# Revit family: Rail-P
name_source: partatom
category: Lighting Fixtures
revit_build: Autodesk Revit 2014 (Build: 20130308_1515(x64)
units: mm (PartAtom-declared; Revit-internal decimal feet)

## types (4) — shared parameters
Apparent Load = 0 VA
Assembly Code = D5020200
Color Filter = 16777215
Default Elevation = 4' - 0"
Description = Rail LED Pendant Indirect/Direct
Dimming Lamp Color Temperature Shift = <None>
Downlight Diffuser = Soft Glow Lens/Blade Baffle with Overlay
Emit Shape Visible in Rendering = No
Emit from Rectangle Length = 0' - 2 1/2"
Fixture Distribution = Indirect/Direct
Glass = Glass - Hubbell - White
Housing Material = Paint - Hubbell - Matte White
Lamp = LED
Load Classification = Lighting
Manufacturer = Litecontrol Lighting
Model = Rail-12L
Mounting = Pendant
Photometric Link = https://www.hubbell.com
Photometric Notes = More IES files download on Photometric Link
Photometric Web File = 11L-P-ID-LPA-04-SOF-Cx-35K-I025-D015.ies
Power Factor = 1
Product Documentation Link = https://hubbellcdn.com
Product Page URL = https://www.hubbell.com
Tilt Angle = -90.00°
Type Comments = Lighting Fixture
URL = https://www.hubbell.com
Uplight distribution = Standard/Low Peak Angle
Voltage = 120 V
Warranty = 5-Years Warranty

## per-type parameters (varying)
| type | Emit from Rectangle Width | zz Length 1 |
| Rail-P-04 | 3' - 8" | 4' - 0" |
| Rail-P-03 | 2' - 8" | 3' - 0" |
| Rail-P-06 | 5' - 8" | 6' - 0" |
| Rail-P-08 | 7' - 8" | 8' - 0" |

## geometry (parser evidence)
native form markers: Sweep x2
no freeform markers — native parametric forms only
